FCSTD DOCUMENT  (FreeCAD 1.0R39109 (Git))
Label: es18bph
License: All rights reserved
LicenseURL: https://en.wikipedia.org/wiki/All_rights_reserved
objects: PartDesign::Body×1, Sketcher::SketchObject×1
note: 3 computed .brp shape members not serialized (recipe doc carries the construction recipe); baked Part::Feature solids carry a one-line shape summary decoded from their .brp

FEATURE [PartDesign::Body] Body
  AllowCompound = false
  Origin = -> Origin
FEATURE [Sketcher::SketchObject] Sketch
  ArcFitTolerance = 1e-06
  FullyConstrained = false
  MakeInternals = false
  Placement = pos=(0,0,0) rot=(0.57735,0.57735,0.57735;2.0944rad)
  sketch-geometry (28):
    g0: LineSegment StartX=0 StartY=0 StartZ=0 EndX=750 EndY=0 EndZ=0
    g1: LineSegment StartX=750 StartY=0 StartZ=0 EndX=750 EndY=18 EndZ=0
    g2: LineSegment StartX=750 StartY=18 StartZ=0 EndX=0 EndY=18 EndZ=0
    g3: LineSegment StartX=0 StartY=18 StartZ=0 EndX=0 EndY=0 EndZ=0
    g4: LineSegment StartX=0 StartY=18 StartZ=0 EndX=18 EndY=18 EndZ=0
    g5: LineSegment StartX=18 StartY=18 StartZ=0 EndX=18 EndY=670 EndZ=0
    g6: LineSegment StartX=18 StartY=670 StartZ=0 EndX=0 EndY=670 EndZ=0
    g7: LineSegment StartX=0 StartY=670 StartZ=0 EndX=0 EndY=18 EndZ=0
    g8: LineSegment StartX=18 StartY=670 StartZ=0 EndX=18 EndY=652 EndZ=0
    g9: LineSegment StartX=18 StartY=652 StartZ=0 EndX=750 EndY=652 EndZ=0
    g10: LineSegment StartX=750 StartY=652 StartZ=0 EndX=750 EndY=670 EndZ=0
    g11: LineSegment StartX=750 StartY=670 StartZ=0 EndX=18 EndY=670 EndZ=0
    g12: GeomPoint X=18 Y=593 Z=0
    g13: GeomPoint X=18 Y=670 Z=0
    g14: LineSegment [constr] StartX=750 StartY=18 StartZ=0 EndX=750 EndY=259 EndZ=0
    g15: LineSegment [constr] StartX=750 StartY=259 StartZ=0 EndX=435 EndY=259 EndZ=0
    g16: LineSegment StartX=435 StartY=259 StartZ=0 EndX=750 EndY=652 EndZ=0
    g17: LineSegment StartX=435 StartY=259 StartZ=0 EndX=420.955 EndY=270.258 EndZ=0
    g18: LineSegment StartX=420.955 StartY=270.258 StartZ=0 EndX=726.932 EndY=652 EndZ=0
    g19: GeomPoint X=432.212 Y=284.303 Z=0
    g20: LineSegment StartX=18 StartY=593 StartZ=0 EndX=432.212 EndY=284.303 EndZ=0
    g21: LineSegment StartX=420.955 StartY=270.258 StartZ=0 EndX=18 EndY=570.565 EndZ=0
    g22: LineSegment [constr] StartX=18 StartY=192.2 StartZ=0 EndX=160 EndY=192.2 EndZ=0
    g23: LineSegment [constr] StartX=160 StartY=17.2003 StartZ=0 EndX=160 EndY=192.2 EndZ=0
    g24: LineSegment StartX=18 StartY=120.53 StartZ=0 EndX=120.531 EndY=18 EndZ=0
    g25: LineSegment StartX=18 StartY=95.0746 StartZ=0 EndX=95.0747 EndY=18 EndZ=0
    g26: LineSegment StartX=435 StartY=259 StartZ=0 EndX=165.796 EndY=175.016 EndZ=0
    g27: LineSegment StartX=165.796 StartY=175.016 StartZ=0 EndX=160.435 EndY=192.2 EndZ=0
  constraints (73):
    c: Coincident(g0,g1)
    c: Coincident(g1,g2)
    c: Coincident(g2,g3)
    c: Coincident(g3,g0)
    c: Horizontal(g0)
    c: Horizontal(g2)
    c: Vertical(g1)
    c: Vertical(g3)
    c: Distance(g1,g3) = 750
    c: Distance(g0,g2) = 18
    c: Coincident(g0,g-1)
    c: Coincident(g4,g5)
    c: Coincident(g5,g6)
    c: Coincident(g6,g7)
    c: Coincident(g7,g4)
    c: Horizontal(g4)
    c: Horizontal(g6)
    c: Vertical(g5)
    c: Vertical(g7)
    c: Distance(g5,g7) = 18
    c: Distance(g4,g6) = 652
    c: Coincident(g4,g2)
    c: Coincident(g8,g9)
    c: Coincident(g9,g10)
    c: Coincident(g10,g11)
    c: Coincident(g11,g8)
    c: Vertical(g8)
    c: Vertical(g10)
    c: Horizontal(g9)
    c: Horizontal(g11)
    c: Distance(g8,g10) = 732
    c: Distance(g9,g11) = 18
    c: Coincident(g8,g5)
    c: PointOnObject(g12,g5)
    c: Coincident(g13,g5)
    c: Distance(g12,g11) = 77
    c: Distance(g14) = 241
    c: Coincident(g14,g1)
    c: Vertical(g14)
    c: Distance(g15) = 315
    c: Coincident(g15,g14)
    c: Horizontal(g15)
    c: Coincident(g16,g15)
    c: Coincident(g16,g9)
    c: Distance(g17) = 18
    c: Coincident(g17,g15)
    c: Angle(g16,g17) = 1.5708
    c: Coincident(g18,g17)
    c: PointOnObject(g18,g9)
    c: Parallel(g18,g16)
    c: PointOnObject(g19,g18)
    c: Distance(g19,g17) = 18
    c: Coincident(g20,g12)
    c: Coincident(g20,g19)
    c: Coincident(g21,g17)
    c: PointOnObject(g21,g5)
    c: Parallel(g21,g20)
    c: Distance(g22) = 142
    c: Horizontal(g22)
    c: PointOnObject(g22,g5)
    c: Vertical(g23)
    c: Distance(g24) = 145
    c: Angle(g-1,g24) = -0.785398
    c: PointOnObject(g24,g5)
    c: PointOnObject(g24,g2)
    c: Parallel(g25,g24)
    c: PointOnObject(g25,g2)
    c: PointOnObject(g25,g5)
    c: Distance(g26) = 282
    c: Coincident(g26,g15)
    c: Distance(g27) = 18
    c: Coincident(g27,g26)
    c: Perpendicular(g26,g27)
